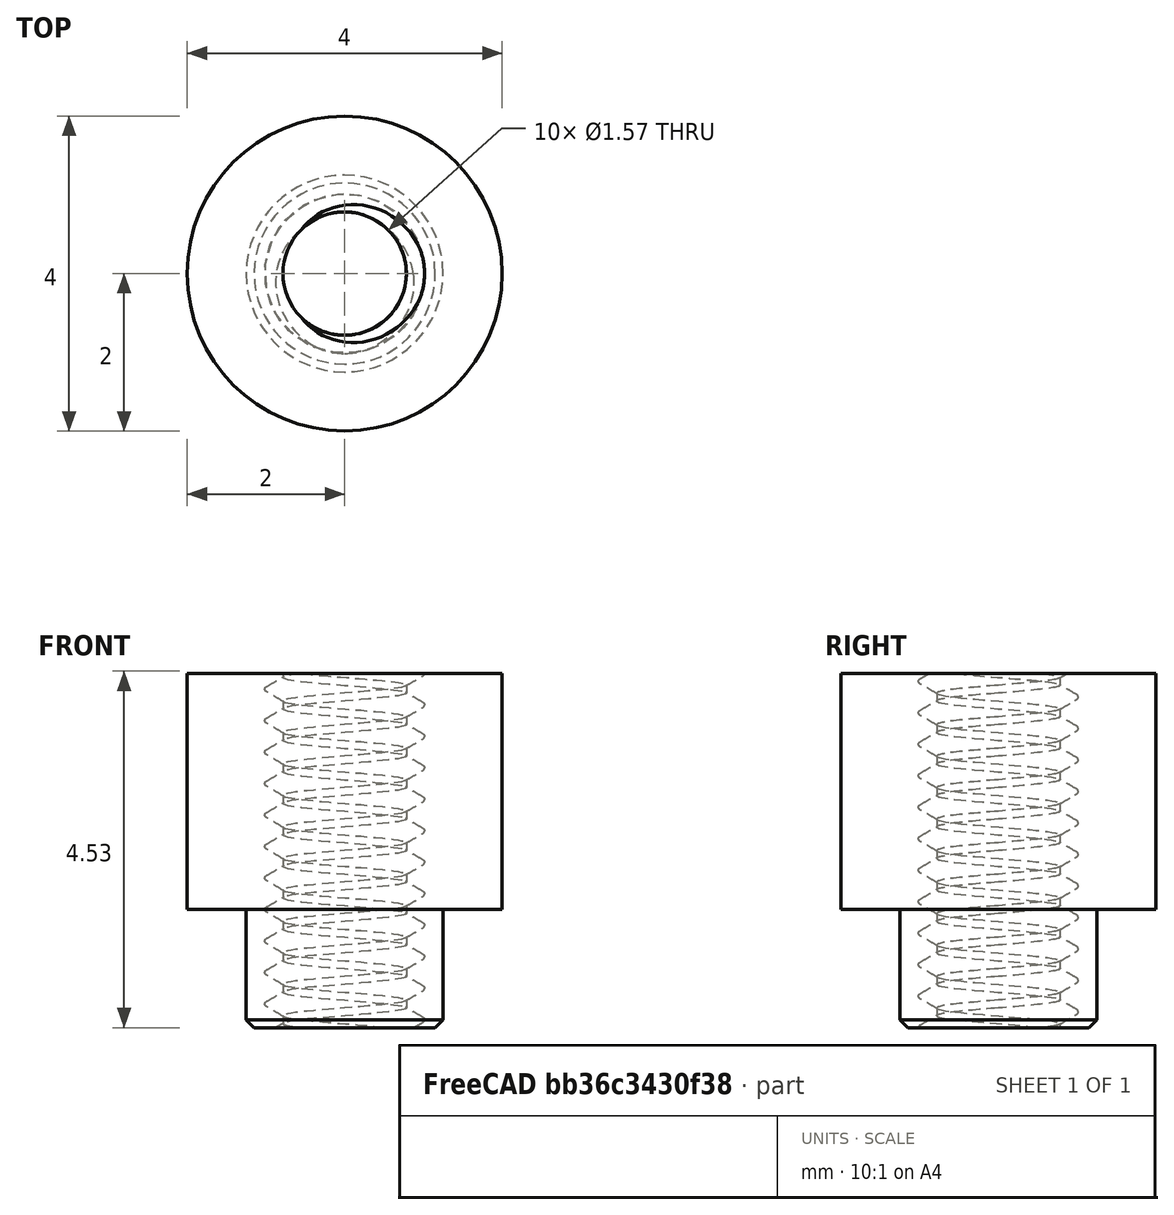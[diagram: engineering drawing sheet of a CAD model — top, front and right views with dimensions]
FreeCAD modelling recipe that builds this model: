
FCSTD DOCUMENT  (FreeCAD 0.21R33771 (Git))
Label: TH-1.6-2.0-M2
License: All rights reserved
LicenseURL: http://en.wikipedia.org/wiki/All_rights_reserved
objects: Part::Cylinder×2, Part::Chamfer×1, Part::FeaturePython×1, Part::MultiFuse×1, Part::Cut×1
note: 6 computed .brp shape members not serialized (recipe doc carries the construction recipe); baked Part::Feature solids carry a one-line shape summary decoded from their .brp

FEATURE [Part::Cylinder] Cylinder  label="円柱"
  Angle = 360
  AttacherType = Attacher::AttachEngine3D
  FirstAngle = 0
  Height = 1.5
  Placement = pos=(0,0,-1.5) rot=(0,0,1;0rad)
  Radius = 1.25
  SecondAngle = 0
FEATURE [Part::Chamfer] Chamfer
  Base = -> Cylinder
  Edges = 1 edges r=0.1: [Edge2]
FEATURE [Part::Cylinder] Cylinder001  label="円柱001"
  Angle = 360
  AttacherType = Attacher::AttachEngine3D
  FirstAngle = 0
  Height = 3
  Radius = 2
  SecondAngle = 0
FEATURE [Part::FeaturePython] ScrewTap  label="M2x20-ScrewTap"  # Fasteners workbench fastener (typed FeaturePython)
  Placement = pos=(0,0,8) rot=(0,0,1;0rad)
  diameter = 2
  diameterCustom = 6
  invert = false
  leftHanded = false
  length = 20
  matchOuter = false
  offset = 0
  pitchCustom = 0.4
  thread = true
  type = 2
FEATURE [Part::MultiFuse] Fusion
  Shapes = -> [Cylinder001,Chamfer]
FEATURE [Part::Cut] Cut
  Base = -> Fusion
  Tool = -> ScrewTap
